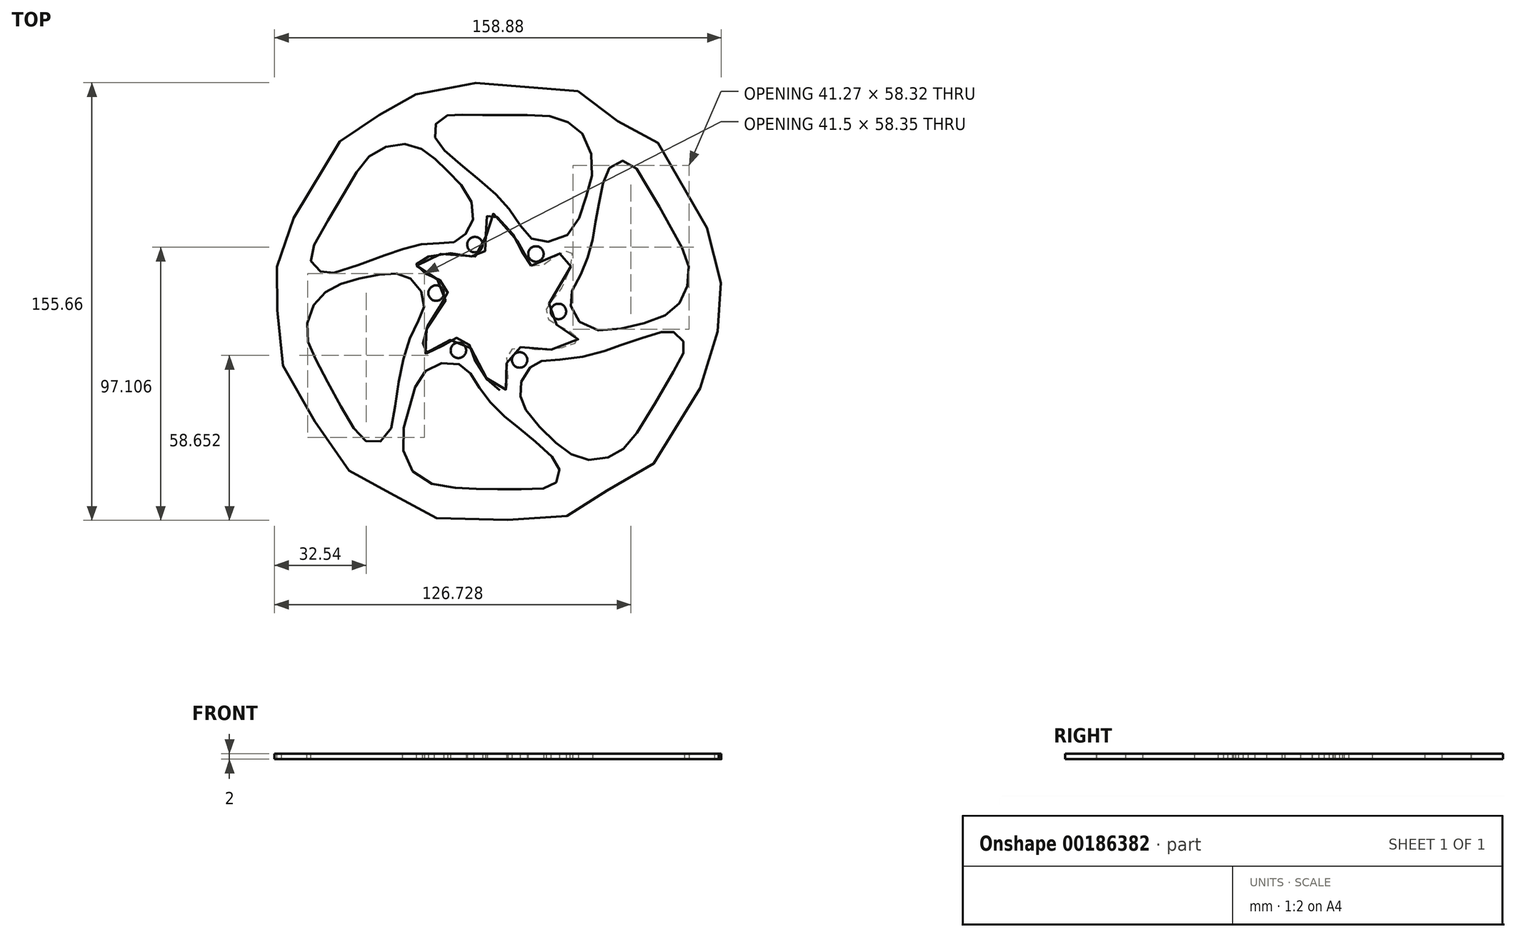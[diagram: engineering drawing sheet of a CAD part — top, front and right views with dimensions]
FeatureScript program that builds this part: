
annotation { "Feature Type Name" : "Feature", "Feature Type Description" : "" }
export const myFeature = defineFeature(function(context is Context, id is Id, definition is map)
    precondition{}
    {
        {
            var Q0;
            Q0=qCreatedBy(makeId("Top.planeOp"),FACE);
            var sketch = newSketch(context, id + "F0", { "sketchPlane" : qUnion([Q0])});
            skPoint(sketch, "E0", {"position": v(15.13, 15.97) * mm});
            skPoint(sketch, "E1", {"position": v(-12.45, -18.31) * mm});
            skCircle(sketch, "E2", {"center": v(15.13, 15.97) * mm, "radius": 2.75 * mm});
            skCircle(sketch, "E3", {"center": v(-12.45, -18.31) * mm, "radius": 2.75 * mm});
            skCircle(sketch, "E4", {"center": v(23.14, -4.47) * mm, "radius": 2.75 * mm});
            skCircle(sketch, "E5", {"center": v(1.38, -1.2) * mm, "radius": 22 * mm, "construction": true});
            skFitSpline(sketch, "E6", {"points": [v(27.7, -55.29) * mm, v(19.97, -49.05) * mm, v(11.68, -39.74) * mm, v(9.68, -34.65) * mm, v(9.94, -29.34) * mm, v(13.8, -23.74) * mm, v(17.66, -22) * mm, v(27.57, -21.3) * mm, v(39.92, -18.44) * mm, v(47.86, -15.58) * mm, v(59.13, -12) * mm, v(63.11, -11.46) * mm, v(66.92, -14.08) * mm, v(67.91, -17.5) * mm, v(65.73, -22.8) * mm, v(50.9, -47.8) * mm, v(44.35, -54.73) * mm, v(35.87, -57.28) * mm, v(27.7, -55.29) * mm]});
            skFitSpline(sketch, "E7", {"points": [v(35.33, 21.1) * mm, v(36.2, 26.68) * mm, v(37.36, 33.06) * mm, v(38.74, 40.02) * mm, v(40.32, 45.24) * mm, v(43.45, 48.36) * mm, v(46.86, 49.01) * mm, v(51, 46.18) * mm, v(55.35, 39) * mm, v(60.2, 30.8) * mm, v(64.78, 22.32) * mm, v(68.55, 14.85) * mm, v(69.56, 8.47) * mm, v(67.9, 1.44) * mm, v(64.63, -3.13) * mm, v(58.9, -6.9) * mm, v(49.62, -9.59) * mm, v(40.4, -11.33) * mm, v(32.21, -9.44) * mm, v(28.22, -4.44) * mm, v(27.2, -0.08) * mm, v(28.51, 3.9) * mm, v(31.63, 9.92) * mm, v(33.66, 15.22) * mm, v(35.33, 21.1) * mm]});
            skFitSpline(sketch, "E8", {"points": [v(-11.1, 65.46) * mm, v(-1.85, 65.44) * mm, v(8.55, 65.4) * mm, v(19.5, 65.06) * mm, v(27, 62.66) * mm, v(32.43, 57.56) * mm, v(35.34, 47.23) * mm, v(33.46, 38.06) * mm, v(29.94, 27.54) * mm, v(24.12, 21.47) * mm, v(15.93, 20.55) * mm, v(11.83, 22.9) * mm, v(7.32, 29.6) * mm, v(2.13, 36.02) * mm, v(-5.2, 42.46) * mm, v(-14.67, 50.44) * mm, v(-19.57, 55.34) * mm, v(-21.1, 59.69) * mm, v(-19.7, 63.23) * mm, v(-15.98, 65.33) * mm, v(-11.1, 65.46) * mm]});
            skFitSpline(sketch, "E9", {"points": [v(-20.77, 49.82) * mm, v(-26.06, 53.6) * mm, v(-32.95, 55.12) * mm, v(-41.5, 52.55) * mm, v(-47.56, 46.8) * mm, v(-55.36, 33.62) * mm, v(-64.54, 17.34) * mm, v(-64.54, 12.71) * mm, v(-60.96, 9.43) * mm, v(-56.8, 9.28) * mm, v(-40.7, 14.8) * mm, v(-31.45, 17.98) * mm, v(-23.64, 19.65) * mm, v(-16.98, 19.8) * mm, v(-12.58, 20.78) * mm, v(-8.87, 24.5) * mm, v(-6.97, 30.04) * mm, v(-9.55, 38) * mm, v(-15.7, 44.9) * mm, v(-20.77, 49.82) * mm]});
            skFitSpline(sketch, "E10", {"points": [v(-54.29, 5.33) * mm, v(-60.38, 1.86) * mm, v(-64.96, -4.24) * mm, v(-66.31, -13.13) * mm, v(-63.45, -20.93) * mm, v(-55.65, -35.58) * mm, v(-48.28, -47.9) * mm, v(-43.51, -51.19) * mm, v(-37.98, -49.16) * mm, v(-35.19, -39.74) * mm, v(-32.98, -25.97) * mm, v(-29.97, -14.84) * mm, v(-26.07, -6.63) * mm, v(-24.53, -1.92) * mm, v(-26.56, 4.1) * mm, v(-31.19, 8.24) * mm, v(-36.55, 9.05) * mm, v(-45.73, 7.75) * mm, v(-54.29, 5.33) * mm]});
            skFitSpline(sketch, "E11", {"points": [v(-13.54, -67.18) * mm, v(-4.57, -67.66) * mm, v(5.24, -67.66) * mm, v(16.41, -67.59) * mm, v(21.49, -66.15) * mm, v(23.22, -63.31) * mm, v(23.22, -59.48) * mm, v(20, -55.44) * mm, v(12.06, -48.26) * mm, v(6.17, -43.67) * mm, v(0.27, -38.25) * mm, v(-4.18, -32.83) * mm, v(-7.54, -27.69) * mm, v(-10.22, -24.26) * mm, v(-15.64, -22.61) * mm, v(-21.8, -24.05) * mm, v(-26.76, -29) * mm, v(-29.51, -37.33) * mm, v(-32.02, -46.27) * mm, v(-31.3, -56.9) * mm, v(-24.64, -64.63) * mm, v(-13.54, -67.18) * mm]});
            skLineSegment(sketch, "E12", {"start": v(15.13, 15.97) * mm, "end": v(-12.45, -18.31) * mm, "construction": true});
            skFitSpline(sketch, "E13", {"points": [v(13.45, 11.75) * mm, v(17.1, 11.8) * mm, v(20.5, 14.18) * mm, v(24.3, 16.47) * mm, v(26.5, 17.13) * mm, v(27.56, 16.82) * mm, v(28.13, 15.28) * mm, v(25.88, 6.99) * mm, v(21.43, 0.02) * mm, v(19.44, -2.14) * mm, v(18.74, -4.43) * mm, v(19.31, -6.85) * mm, v(21.6, -8.84) * mm, v(25.35, -10.43) * mm, v(27.86, -12.01) * mm, v(29.58, -13.47) * mm, v(30.16, -14.66) * mm, v(29.23, -15.67) * mm, v(25.7, -17.13) * mm, v(20.63, -18.05) * mm, v(16.14, -18.14) * mm, v(12.83, -17.74) * mm, v(9.57, -17.17) * mm, v(6.75, -17.83) * mm, v(5.11, -19.68) * mm, v(4.63, -21.62) * mm, v(4.85, -23.6) * mm, v(5.16, -27.05) * mm, v(4.98, -30.53) * mm, v(4.63, -31.98) * mm, v(3.75, -32.73) * mm, v(2.3, -32.51) * mm, v(0.49, -31.1) * mm, v(-2.03, -28.77) * mm, v(-5.69, -23.6) * mm, v(-7.5, -19.6) * mm, v(-8.11, -17.17) * mm, v(-9.35, -15.19) * mm, v(-11.64, -13.95) * mm, v(-14.42, -14.17) * mm, v(-16.66, -15.67) * mm, v(-20.15, -17.96) * mm, v(-23.06, -19.24) * mm, v(-24.56, -19.24) * mm, v(-25.26, -17.79) * mm, v(-24.95, -15.19) * mm, v(-24.03, -11.53) * mm, v(-22.66, -8.18) * mm, v(-19.4, -3.15) * mm, v(-17.02, -0.42) * mm, v(-16.22, 2.67) * mm, v(-17.41, 5.5) * mm, v(-19.15, 6.7) * mm, v(-21.07, 7.39) * mm, v(-24.03, 8.93) * mm, v(-26.36, 10.56) * mm, v(-27.25, 11.66) * mm, v(-27.33, 12.68) * mm, v(-26.19, 13.87) * mm, v(-21.95, 15.32) * mm, v(-16.53, 16.25) * mm, v(-10.98, 15.9) * mm, v(-7.23, 15.06) * mm, v(-4.63, 15.54) * mm, v(-2.73, 17.4) * mm, v(-2.2, 19.82) * mm, v(-2.78, 24.05) * mm, v(-2.47, 28.42) * mm, v(-1.98, 29.91) * mm, v(-0.4, 30.4) * mm, v(1.2, 29.34) * mm, v(4.94, 25.81) * mm, v(8.77, 20.04) * mm, v(10.18, 16.82) * mm, v(10.98, 14.22) * mm, v(13.45, 11.75) * mm]});
            skFitSpline(sketch, "E14", {"points": [v(75.9, 25.27) * mm, v(61.18, 51.52) * mm, v(57.69, 56.32) * mm, v(52.45, 60.12) * mm, v(47.9, 61.74) * mm, v(43.97, 63.36) * mm, v(40.67, 65.92) * mm, v(36.3, 70.16) * mm, v(30.13, 73.9) * mm, v(21.28, 76.2) * mm, v(-15.45, 76.7) * mm, v(-21.3, 76.02) * mm, v(-25.98, 73.84) * mm, v(-29.85, 70.97) * mm, v(-32.97, 68.1) * mm, v(-36.58, 66.35) * mm, v(-41.2, 65.23) * mm, v(-47.24, 62.49) * mm, v(-51.05, 59.5) * mm, v(-54.48, 56.07) * mm, v(-58.4, 50.14) * mm, v(-72, 27.2) * mm, v(-75.74, 20.47) * mm, v(-76.8, 15.98) * mm, v(-76.92, 10.55) * mm, v(-75.92, 6.56) * mm, v(-75.55, 2.07) * mm, v(-76.55, -2.73) * mm, v(-77.73, -9.46) * mm, v(-77.3, -16.2) * mm, v(-74.43, -24.43) * mm, v(-71.37, -29.6) * mm, v(-66.76, -37.77) * mm, v(-58.1, -53.23) * mm, v(-55.41, -57.35) * mm, v(-51.6, -60.84) * mm, v(-46, -63.77) * mm, v(-42.32, -64.64) * mm, v(-37.9, -67.88) * mm, v(-33.46, -72.18) * mm, v(-29.23, -74.93) * mm, v(-20.93, -77.86) * mm, v(-14.57, -78.36) * mm, v(-1.54, -78.54) * mm, v(15.85, -78.73) * mm, v(20.4, -78.67) * mm, v(26.14, -77.24) * mm, v(32, -73.3) * mm, v(35.24, -70.5) * mm, v(39.36, -68.57) * mm, v(44.66, -67.13) * mm, v(50.08, -64.58) * mm, v(57.13, -58.34) * mm, v(63.61, -48.43) * mm, v(75.96, -27.67) * mm, v(79.2, -21.06) * mm, v(80.07, -13.27) * mm, v(78.89, -8.21) * mm, v(78.83, -3.16) * mm, v(80.45, 3.44) * mm, v(80.88, 10.99) * mm, v(78.26, 20.78) * mm, v(75.9, 25.27) * mm]});
            skLineSegment(sketch, "E15", {"start": v(9.33, -21.72) * mm, "end": v(-6.57, 19.31) * mm, "construction": true});
            skCircle(sketch, "E16", {"center": v(-6.57, 19.31) * mm, "radius": 2.75 * mm});
            skCircle(sketch, "E17", {"center": v(9.33, -21.72) * mm, "radius": 2.75 * mm});
            skLineSegment(sketch, "E18", {"start": v(23.14, -4.47) * mm, "end": v(-20.37, 2.07) * mm, "construction": true});
            skCircle(sketch, "E19", {"center": v(-20.37, 2.07) * mm, "radius": 2.75 * mm});
            skSolve(sketch);
        }
        {
            var Q0;
            Q0 = qSketchRegion(id + "F0", true);
            extrude(context, id + "F1", {"entities" : qUnion([Q0]), "depth" : 2 * mm, "offsetDistance" : 25 * mm});
        }
    });
